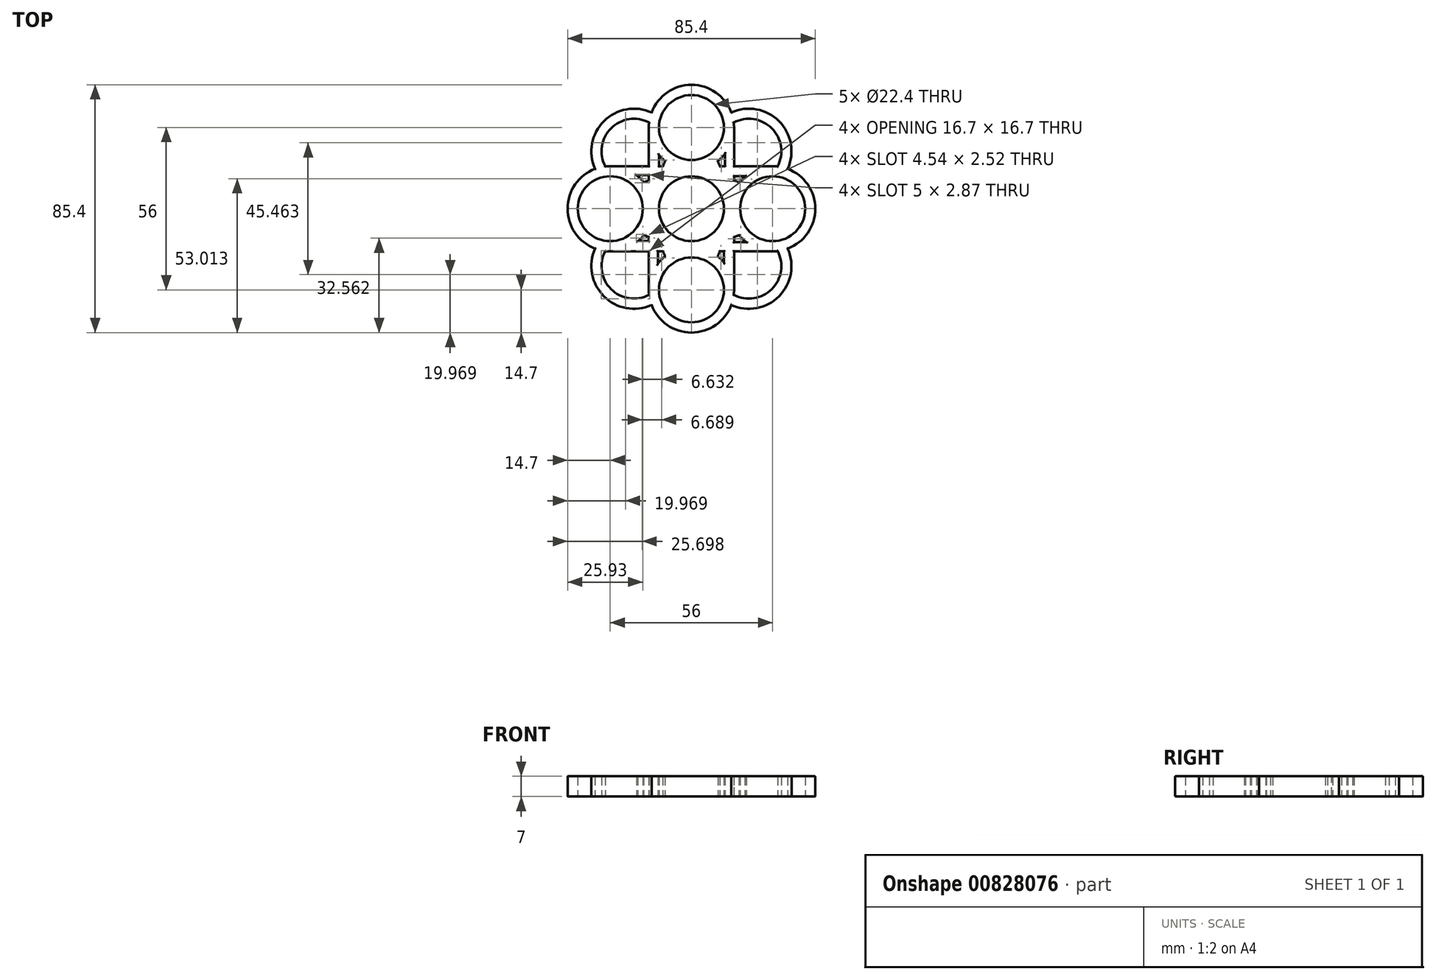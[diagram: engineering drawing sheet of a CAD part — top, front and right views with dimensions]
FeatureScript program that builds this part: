
annotation { "Feature Type Name" : "Feature", "Feature Type Description" : "" }
export const myFeature = defineFeature(function(context is Context, id is Id, definition is map)
    precondition{}
    {
        {
            var Q0;
            Q0=qCreatedBy(makeId("Top.planeOp"),FACE);
            var sketch = newSketch(context, id + "F0", { "sketchPlane" : qUnion([Q0])});
            skCircle(sketch, "E0", {"center": v(0, 0) * mm, "radius": 11.2 * mm});
            skCircle(sketch, "E1", {"center": v(0, 28) * mm, "radius": 11.2 * mm});
            skArc(sketch, "E2.0", {"start": v(-4.48, 14) * mm, "mid": v(-8.15, 12.23) * mm, "end": v(-11.2, 9.52) * mm});
            skLineSegment(sketch, "E3", {"start": v(14.7, 0) * mm, "end": v(14.7, 28) * mm});
            skLineSegment(sketch, "E4", {"start": v(-14.7, 28) * mm, "end": v(-14.7, 0) * mm});
            skLineSegment(sketch, "E5.0", {"start": v(11.55, 9.1) * mm, "end": v(11.55, 18.9) * mm});
            skLineSegment(sketch, "E6.0", {"start": v(-11.2, 18.48) * mm, "end": v(-11.2, 9.52) * mm});
            skArc(sketch, "E7.trimOffspring", {"start": v(11.55, 9.1) * mm, "mid": v(8.38, 12.08) * mm, "end": v(4.48, 14) * mm});
            skArc(sketch, "E8.trimOffspring", {"start": v(-14.7, 0) * mm, "mid": v(0, -14.7) * mm, "end": v(14.7, 0) * mm});
            skArc(sketch, "E9.0", {"start": v(-11.2, 18.48) * mm, "mid": v(-8.15, 15.77) * mm, "end": v(-4.48, 14) * mm});
            skArc(sketch, "E10.trimOffspring", {"start": v(4.48, 14) * mm, "mid": v(8.38, 15.92) * mm, "end": v(11.55, 18.9) * mm});
            skArc(sketch, "E11.trimOffspring", {"start": v(14.7, 28) * mm, "mid": v(0, 42.7) * mm, "end": v(-14.7, 28) * mm});
            skSolve(sketch);
        }
        {
            var Q0;
            Q0=qCreatedBy(makeId("Right.planeOp"),FACE);
            var sketch = newSketch(context, id + "F1", { "sketchPlane" : qUnion([Q0])});
            skLineSegment(sketch, "E12", {"start": v(0, 0) * mm, "end": v(0, 21.05) * mm, "construction": true});
            skSolve(sketch);
        }
        {
            var Q0;
            Q0=makeQuery(id+"F0.imprint","IMPRINT",FACE,{"disambiguationData":[TD([[makeQuery(id+"F0.imprint","IMPRINT",EDGE,{"derivedFrom":sQuery(id+"F0.wireOp",EDGE,"E0")}),-1.0]])]});
            extrude(context, id + "F2", {"entities" : qUnion([Q0]), "depth" : 7 * mm, "offsetDistance" : 25 * mm});
        }
        {
            var Q0;
            Q0=makeQuery(id+"F2.opExtrude","SWEPT_BODY",BODY,{"disambiguationData":[OSD([sQuery(id+"F0.wireOp",EDGE,"E0"),sQuery(id+"F0.wireOp",EDGE,"E1"),sQuery(id+"F0.wireOp",EDGE,"1ab0b98d-e761-4363-9e53-99a3b5d04243.0"),sQuery(id+"F0.wireOp",EDGE,"E2.0"),sQuery(id+"F0.wireOp",EDGE,"E3"),sQuery(id+"F0.wireOp",EDGE,"E4"),sQuery(id+"F0.wireOp",EDGE,"E5.0"),sQuery(id+"F0.wireOp",EDGE,"E6.0"),sQuery(id+"F0.wireOp",EDGE,"cab20ea3-4361-4bd5-b0ff-d3af068d0fd7.trimOffspring"),sQuery(id+"F0.wireOp",EDGE,"E7.trimOffspring"),sQuery(id+"F0.wireOp",EDGE,"32100815-3d8e-4623-8c92-91c9ed5b2969.trimOffspring"),sQuery(id+"F0.wireOp",EDGE,"E8.trimOffspring")])]});
            var Q1;
            Q1=sQuery(id+"F1.wireOp",EDGE,"E12");
            circularPattern(context, id + "F3", {"operationType" : NewBodyOperationType.ADD, "entities" : qUnion([Q0]), "axis" : qUnion([Q1]), "angle" : 360 * degree, "instanceCount" : 8, "equalSpace" : true});
        }
        {
            var Q0;
            {var subQ0=makeQuery(id+"F2.opExtrude","CAP_FACE",FACE,{"disambiguationData":[OSD([sQuery(id+"F0.wireOp",EDGE,"E0"),sQuery(id+"F0.wireOp",EDGE,"E1"),sQuery(id+"F0.wireOp",EDGE,"E2.0"),sQuery(id+"F0.wireOp",EDGE,"E3"),sQuery(id+"F0.wireOp",EDGE,"E4"),sQuery(id+"F0.wireOp",EDGE,"E5.0"),sQuery(id+"F0.wireOp",EDGE,"E6.0"),sQuery(id+"F0.wireOp",EDGE,"E7.trimOffspring"),sQuery(id+"F0.wireOp",EDGE,"E8.trimOffspring"),sQuery(id+"F0.wireOp",EDGE,"E9.0"),sQuery(id+"F0.wireOp",EDGE,"E10.trimOffspring"),sQuery(id+"F0.wireOp",EDGE,"E11.trimOffspring")])],"isStart":false});Q0=makeQuery(id+"F3.boolean.opBoolean","MERGE",FACE,{"derivedFrom":[subQ0,makeQuery(id+"F3.opPattern","COPY",FACE,{"derivedFrom":subQ0,"instanceName":"1"}),makeQuery(id+"F3.opPattern","COPY",FACE,{"derivedFrom":subQ0,"instanceName":"2"}),makeQuery(id+"F3.opPattern","COPY",FACE,{"derivedFrom":subQ0,"instanceName":"3"}),makeQuery(id+"F3.opPattern","COPY",FACE,{"derivedFrom":subQ0,"instanceName":"4"}),makeQuery(id+"F3.opPattern","COPY",FACE,{"derivedFrom":subQ0,"instanceName":"5"}),makeQuery(id+"F3.opPattern","COPY",FACE,{"derivedFrom":subQ0,"instanceName":"6"}),makeQuery(id+"F3.opPattern","COPY",FACE,{"derivedFrom":subQ0,"instanceName":"7"})]});}
            var sketch = newSketch(context, id + "F4", { "sketchPlane" : qUnion([Q0])});
            skCircle(sketch, "E13.0", {"center": v(0, 28) * mm, "radius": 11.2 * mm});
            skCircle(sketch, "E14.1.0", {"center": v(-28, 0) * mm, "radius": 11.2 * mm});
            skCircle(sketch, "E14.2.0", {"center": v(0, -28) * mm, "radius": 11.2 * mm});
            skCircle(sketch, "E14.3.0", {"center": v(28, 0) * mm, "radius": 11.2 * mm});
            skPoint(sketch, "E14.center", {"position": v(0, 0) * mm});
            skSolve(sketch);
        }
        {
            var Q0;
            Q0 = qSketchRegion(id + "F4", true);
            extrude(context, id + "F5", {"entities" : qUnion([Q0]), "operationType" : NewBodyOperationType.REMOVE, "endBound" : BoundingType.THROUGH_ALL, "oppositeDirection" : true, "depth" : 25 * mm, "offsetDistance" : 25 * mm});
        }
        {
            var Q0;
            Q0=makeQuery(id+"F2.opExtrude","CAP_FACE",FACE,{"disambiguationData":[OSD([sQuery(id+"F0.wireOp",EDGE,"E0"),sQuery(id+"F0.wireOp",EDGE,"E1"),sQuery(id+"F0.wireOp",EDGE,"E2.0"),sQuery(id+"F0.wireOp",EDGE,"E3"),sQuery(id+"F0.wireOp",EDGE,"E4"),sQuery(id+"F0.wireOp",EDGE,"E5.0"),sQuery(id+"F0.wireOp",EDGE,"E6.0"),sQuery(id+"F0.wireOp",EDGE,"E7.trimOffspring"),sQuery(id+"F0.wireOp",EDGE,"E8.trimOffspring"),sQuery(id+"F0.wireOp",EDGE,"E9.0"),sQuery(id+"F0.wireOp",EDGE,"E10.trimOffspring"),sQuery(id+"F0.wireOp",EDGE,"E11.trimOffspring")])],"isStart":false});
            var Q1;
            Q1=makeQuery(id+"F2.opExtrude","CAP_FACE",FACE,{"disambiguationData":[OSD([sQuery(id+"F0.wireOp",EDGE,"E0"),sQuery(id+"F0.wireOp",EDGE,"E1"),sQuery(id+"F0.wireOp",EDGE,"E2.0"),sQuery(id+"F0.wireOp",EDGE,"E3"),sQuery(id+"F0.wireOp",EDGE,"E4"),sQuery(id+"F0.wireOp",EDGE,"E5.0"),sQuery(id+"F0.wireOp",EDGE,"E6.0"),sQuery(id+"F0.wireOp",EDGE,"E7.trimOffspring"),sQuery(id+"F0.wireOp",EDGE,"E8.trimOffspring"),sQuery(id+"F0.wireOp",EDGE,"E9.0"),sQuery(id+"F0.wireOp",EDGE,"E10.trimOffspring"),sQuery(id+"F0.wireOp",EDGE,"E11.trimOffspring")])],"isStart":true});
            fillet(context, id + "F6", {"entities" : qUnion([Q0, Q1]), "radius" : 0.2 * mm, "tangentPropagation" : true, "allowEdgeOverflow" : false});
        }
    });
